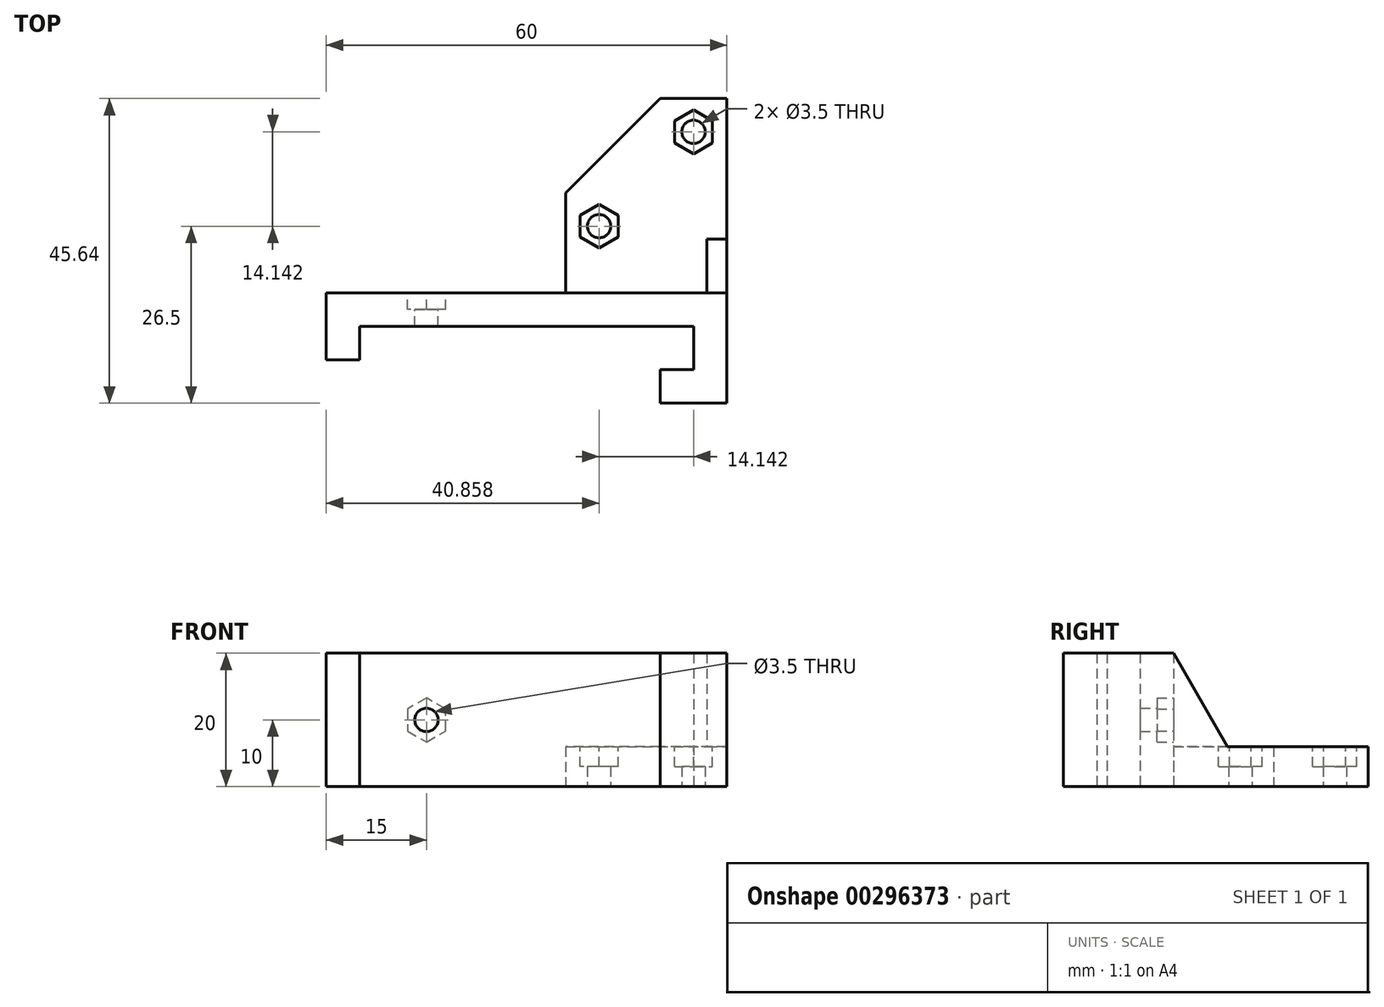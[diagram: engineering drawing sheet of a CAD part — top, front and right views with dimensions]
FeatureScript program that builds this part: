
annotation { "Feature Type Name" : "Feature", "Feature Type Description" : "" }
export const myFeature = defineFeature(function(context is Context, id is Id, definition is map)
    precondition{}
    {
        {
            var Q0;
            Q0=qCreatedBy(makeId("Top.planeOp"),FACE);
            var sketch = newSketch(context, id + "F0", { "sketchPlane" : qUnion([Q0])});
            skLineSegment(sketch, "E0", {"start": v(0, 0) * mm, "end": v(0, 10) * mm});
            skLineSegment(sketch, "E1", {"start": v(0, 10) * mm, "end": v(60, 10) * mm});
            skLineSegment(sketch, "E2", {"start": v(60, 10) * mm, "end": v(60, -6.5) * mm});
            skLineSegment(sketch, "E3", {"start": v(60, -6.5) * mm, "end": v(50, -6.5) * mm});
            skLineSegment(sketch, "E4", {"start": v(50, -6.5) * mm, "end": v(50, -1.5) * mm});
            skLineSegment(sketch, "E5", {"start": v(50, -1.5) * mm, "end": v(55, -1.5) * mm});
            skLineSegment(sketch, "E6", {"start": v(55, -1.5) * mm, "end": v(55, 5) * mm});
            skLineSegment(sketch, "E7", {"start": v(55, 5) * mm, "end": v(5, 5) * mm});
            skLineSegment(sketch, "E8", {"start": v(5, 5) * mm, "end": v(5, 0) * mm});
            skLineSegment(sketch, "E9", {"start": v(5, 0) * mm, "end": v(0, 0) * mm});
            skSolve(sketch);
        }
        {
            var Q0;
            Q0 = qSketchRegion(id + "F0", true);
            extrude(context, id + "F1", {"entities" : qUnion([Q0]), "depth" : 20 * mm});
        }
        {
            var Q0;
            Q0=makeQuery(id+"F1.opExtrude","CAP_FACE",FACE,{"disambiguationData":[OSD([sQuery(id+"F0.wireOp",EDGE,"E0"),sQuery(id+"F0.wireOp",EDGE,"E1"),sQuery(id+"F0.wireOp",EDGE,"E2"),sQuery(id+"F0.wireOp",EDGE,"E3"),sQuery(id+"F0.wireOp",EDGE,"E4"),sQuery(id+"F0.wireOp",EDGE,"E5"),sQuery(id+"F0.wireOp",EDGE,"E6"),sQuery(id+"F0.wireOp",EDGE,"E7"),sQuery(id+"F0.wireOp",EDGE,"E8"),sQuery(id+"F0.wireOp",EDGE,"E9")])],"isStart":true});
            var sketch = newSketch(context, id + "F2", { "sketchPlane" : qUnion([Q0])});
            skLineSegment(sketch, "E10", {"start": v(60, -10) * mm, "end": v(60, -39.14) * mm});
            skLineSegment(sketch, "E11", {"start": v(60, -39.14) * mm, "end": v(50, -39.14) * mm});
            skLineSegment(sketch, "E12", {"start": v(50, -39.14) * mm, "end": v(35.86, -25) * mm});
            skLineSegment(sketch, "E13", {"start": v(35.86, -25) * mm, "end": v(35.86, -10) * mm});
            skLineSegment(sketch, "E14", {"start": v(35.86, -10) * mm, "end": v(60, -10) * mm});
            skCircle(sketch, "E15", {"center": v(40.86, -20) * mm, "radius": 1.75 * mm});
            skCircle(sketch, "E16", {"center": v(55, -34.14) * mm, "radius": 1.75 * mm});
            skLineSegment(sketch, "E17", {"start": v(55, -34.14) * mm, "end": v(40.86, -20) * mm, "construction": true});
            skSolve(sketch);
        }
        {
            var Q0;
            Q0 = qSketchRegion(id + "F2", true);
            extrude(context, id + "F3", {"entities" : qUnion([Q0]), "operationType" : NewBodyOperationType.ADD, "oppositeDirection" : true, "depth" : 6 * mm});
        }
        {
            var Q0;
            Q0=makeQuery(id+"F3.opExtrude","CAP_FACE",FACE,{"disambiguationData":[OSD([sQuery(id+"F2.wireOp",EDGE,"E10"),sQuery(id+"F2.wireOp",EDGE,"E11"),sQuery(id+"F2.wireOp",EDGE,"E12"),sQuery(id+"F2.wireOp",EDGE,"E13"),sQuery(id+"F2.wireOp",EDGE,"E14"),sQuery(id+"F2.wireOp",EDGE,"E15"),sQuery(id+"F2.wireOp",EDGE,"E16")])],"isStart":false});
            var sketch = newSketch(context, id + "F4", { "sketchPlane" : qUnion([Q0])});
            skCircle(sketch, "E18.cCircle", {"center": v(40.86, 20) * mm, "radius": 2.85 * mm, "construction": true});
            skLineSegment(sketch, "E18.0", {"start": v(38, 18.35) * mm, "end": v(38, 21.65) * mm});
            skLineSegment(sketch, "E18.1", {"start": v(38, 21.65) * mm, "end": v(40.86, 23.3) * mm});
            skLineSegment(sketch, "E18.2", {"start": v(40.86, 23.3) * mm, "end": v(43.7, 21.65) * mm});
            skLineSegment(sketch, "E18.3", {"start": v(43.7, 21.65) * mm, "end": v(43.7, 18.35) * mm});
            skLineSegment(sketch, "E18.4", {"start": v(43.7, 18.35) * mm, "end": v(40.86, 16.7) * mm});
            skLineSegment(sketch, "E18.5", {"start": v(40.86, 16.7) * mm, "end": v(38, 18.35) * mm});
            skPoint(sketch, "E18.0.midPoint", {"position": v(38, 20) * mm});
            skCircle(sketch, "E19.cCircle", {"center": v(55, 34.14) * mm, "radius": 2.85 * mm, "construction": true});
            skLineSegment(sketch, "E19.0", {"start": v(57.85, 35.79) * mm, "end": v(57.85, 32.5) * mm});
            skLineSegment(sketch, "E19.1", {"start": v(57.85, 32.5) * mm, "end": v(55, 30.85) * mm});
            skLineSegment(sketch, "E19.2", {"start": v(55, 30.85) * mm, "end": v(52.15, 32.5) * mm});
            skLineSegment(sketch, "E19.3", {"start": v(52.15, 32.5) * mm, "end": v(52.15, 35.79) * mm});
            skLineSegment(sketch, "E19.4", {"start": v(52.15, 35.79) * mm, "end": v(55, 37.43) * mm});
            skLineSegment(sketch, "E19.5", {"start": v(55, 37.43) * mm, "end": v(57.85, 35.79) * mm});
            skPoint(sketch, "E19.0.midPoint", {"position": v(57.85, 34.14) * mm});
            skSolve(sketch);
        }
        {
            var Q0;
            Q0 = qSketchRegion(id + "F4", true);
            extrude(context, id + "F5", {"entities" : qUnion([Q0]), "operationType" : NewBodyOperationType.REMOVE, "oppositeDirection" : true, "depth" : 3 * mm});
        }
        {
            var Q0;
            Q0=makeQuery(id+"F3.boolean.opBoolean","MERGE",FACE,{"derivedFrom":[makeQuery(id+"F1.opExtrude","SWEPT_FACE",FACE,{"disambiguationData":[OSD([sQuery(id+"F0.wireOp",EDGE,"E2")])]}),makeQuery(id+"F3.opExtrude","SWEPT_FACE",FACE,{"disambiguationData":[OSD([sQuery(id+"F2.wireOp",EDGE,"E10")])]})]});
            var sketch = newSketch(context, id + "F6", { "sketchPlane" : qUnion([Q0])});
            skLineSegment(sketch, "E20", {"start": v(10, 20) * mm, "end": v(18.08, 6) * mm});
            skLineSegment(sketch, "E21", {"start": v(18.08, 6) * mm, "end": v(10, 6) * mm});
            skLineSegment(sketch, "E22", {"start": v(10, 6) * mm, "end": v(10, 20) * mm});
            skSolve(sketch);
        }
        {
            var Q0;
            Q0 = qSketchRegion(id + "F6", true);
            extrude(context, id + "F7", {"entities" : qUnion([Q0]), "operationType" : NewBodyOperationType.ADD, "oppositeDirection" : true, "depth" : 3 * mm});
        }
        {
            var Q0;
            Q0=makeQuery(id+"F1.opExtrude","SWEPT_FACE",FACE,{"disambiguationData":[OSD([sQuery(id+"F0.wireOp",EDGE,"E1")])]});
            var sketch = newSketch(context, id + "F8", { "sketchPlane" : qUnion([Q0])});
            skCircle(sketch, "E23", {"center": v(-15, 10) * mm, "radius": 1.75 * mm});
            skPoint(sketch, "E23.centerSnap0", {"position": v(0, 10) * mm});
            skSolve(sketch);
        }
        {
            var Q0;
            Q0 = qSketchRegion(id + "F8", true);
            extrude(context, id + "F9", {"entities" : qUnion([Q0]), "operationType" : NewBodyOperationType.REMOVE, "endBound" : BoundingType.THROUGH_ALL, "oppositeDirection" : true, "depth" : 25 * mm});
        }
        {
            var Q0;
            Q0=makeQuery(id+"F1.opExtrude","SWEPT_FACE",FACE,{"disambiguationData":[OSD([sQuery(id+"F0.wireOp",EDGE,"E1")])]});
            var sketch = newSketch(context, id + "F10", { "sketchPlane" : qUnion([Q0])});
            skCircle(sketch, "E24.cCircle", {"center": v(-15, 10) * mm, "radius": 2.85 * mm, "construction": true});
            skLineSegment(sketch, "E24.0", {"start": v(-12.15, 11.65) * mm, "end": v(-12.15, 8.35) * mm});
            skLineSegment(sketch, "E24.1", {"start": v(-12.15, 8.35) * mm, "end": v(-15, 6.7) * mm});
            skLineSegment(sketch, "E24.2", {"start": v(-15, 6.7) * mm, "end": v(-17.85, 8.35) * mm});
            skLineSegment(sketch, "E24.3", {"start": v(-17.85, 8.35) * mm, "end": v(-17.85, 11.65) * mm});
            skLineSegment(sketch, "E24.4", {"start": v(-17.85, 11.65) * mm, "end": v(-15, 13.3) * mm});
            skLineSegment(sketch, "E24.5", {"start": v(-15, 13.3) * mm, "end": v(-12.15, 11.65) * mm});
            skPoint(sketch, "E24.0.midPoint", {"position": v(-12.15, 10) * mm});
            skSolve(sketch);
        }
        {
            var Q0;
            Q0 = qSketchRegion(id + "F10", true);
            extrude(context, id + "F11", {"entities" : qUnion([Q0]), "operationType" : NewBodyOperationType.REMOVE, "oppositeDirection" : true, "depth" : 2.5 * mm});
        }
    });
